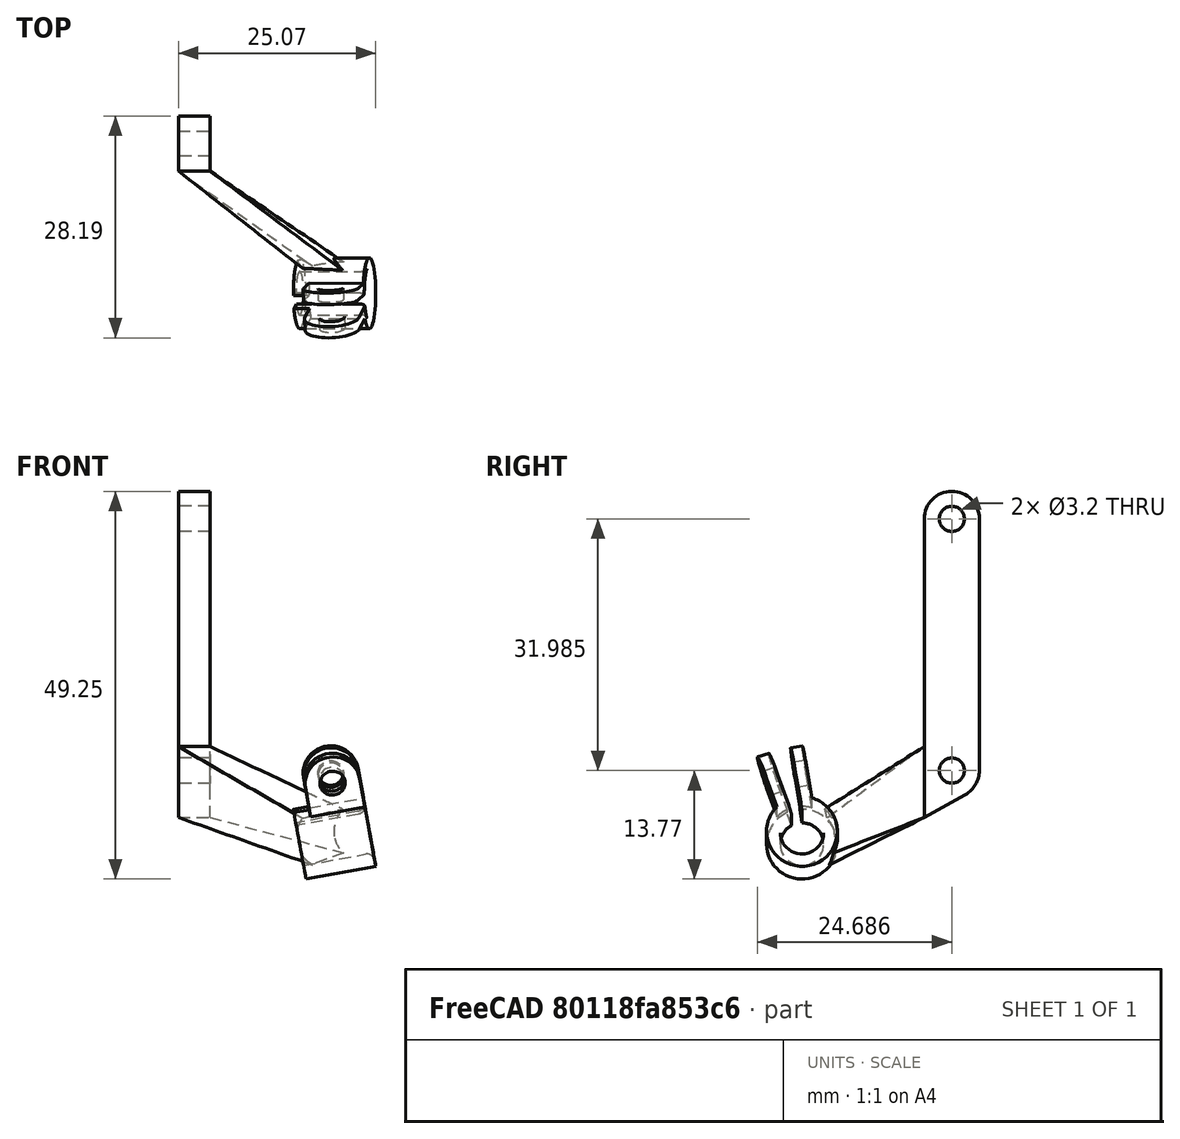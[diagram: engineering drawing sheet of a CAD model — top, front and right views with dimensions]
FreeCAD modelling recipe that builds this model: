
FCSTD DOCUMENT  (FreeCAD 0.19R21097 (Git))
Label: mount
License: All rights reserved
LicenseURL: http://en.wikipedia.org/wiki/All_rights_reserved
objects: Sketcher::SketchObject×8, PartDesign::Plane×6, Part::Extrusion×4, Part::MultiFuse×2, Mesh::Feature×1, Part::Feature×1, PartDesign::Pad×1, PartDesign::Body×1, Part::Sweep×1, Part::Cut×1, Part::Fillet×1
note: 27 computed .brp shape members not serialized (recipe doc carries the construction recipe); baked Part::Feature solids carry a one-line shape summary decoded from their .brp

FEATURE [Mesh::Feature] MK3S_nozzle_camera_mount_screw_tight
  Placement = pos=(-2,363,-102) rot=(0,0,1;3.14159rad)
FEATURE [Sketcher::SketchObject] Sketch  label="base arm top"
  MapMode = 5
  Placement = pos=(0,0,0) rot=(0.57735,0.57735,0.57735;2.0944rad)
  Support = -> [YZ_Plane]
  sketch-geometry (7):
    g0: Circle CenterX=3.46624 CenterY=28.9348 CenterZ=0 NormalX=0 NormalY=0 NormalZ=1 AngleXU=0 Radius=1.6
    g1: Circle CenterX=3.46624 CenterY=-3.05053 CenterZ=0 NormalX=0 NormalY=0 NormalZ=1 AngleXU=0 Radius=1.6
    g2: LineSegment StartX=-0.03376 StartY=28.9348 StartZ=0 EndX=-0.03376 EndY=-9.00443 EndZ=0
    g3: LineSegment StartX=6.96624 StartY=28.9348 StartZ=0 EndX=6.96624 EndY=-3.05053 EndZ=0
    g4: ArcOfCircle CenterX=3.46624 CenterY=28.9348 CenterZ=0 NormalX=0 NormalY=0 NormalZ=1 AngleXU=0 Radius=3.5 StartAngle=0 EndAngle=3.14159
    g5: ArcOfCircle CenterX=3.46624 CenterY=-3.05053 CenterZ=0 NormalX=0 NormalY=0 NormalZ=1 AngleXU=0 Radius=3.5 StartAngle=5.22031 EndAngle=6.28319
    g6: LineSegment StartX=-0.03376 StartY=-9.00443 StartZ=0 EndX=5.16851 EndY=-6.10868 EndZ=0
  constraints (18):
    c: Equal(g0,g1) = 3.2
    c: Vertical(g2)
    c: Vertical(g3)
    c: Horizontal(g3,g0)
    c: Horizontal(g0,g2)
    c: Coincident(g5,g1)
    c: Coincident(g3,g4)
    c: Coincident(g2,g4)
    c: Coincident(g4,g0)
    c: DistanceX(g0,g3) = 3.5
    c: Vertical(g0,g1)
    c: Diameter(g1) = 3.2
    c: Tangent(g5,g3) = 1.5708
    c: Coincident(g6,g2)
    c: Tangent(g6,g5) = -1.5708
    c: DistanceX(g0) = 3.46624
    c: DistanceY(g0) = 28.9348
    c: DistanceY(g1) = -3.05053
FEATURE [Part::Feature] MK3S_nozzle_camera_mount_screw_tight001
  Placement = pos=(6.10201,-725.648,-5.94582) rot=(0,0,1;0rad)
  shape: bbox 25.16 x 32.85 x 50.81 mm, 5956 faces, 0 solids (baked)
FEATURE [PartDesign::Plane] DatumPlane  label="DatumPlane grab top"
  AttachmentOffset = pos=(-24,-30,-2) rot=(0.379352,0.080641,0.921732;0.453327rad)
  Length = 87.983
  MapMode = 45
  Placement = pos=(26.7496,-49.7619,-24.5712) rot=(0.538842,0.541154,0.645602;1.98935rad)
  ResizeMode = 0
  Support = -> [MK3S_nozzle_camera_mount_screw_tight001]
  Width = 71.6948
FEATURE [Sketcher::SketchObject] Sketch001  label="grab top"
  MapMode = 5
  Placement = pos=(26.7496,-49.7619,-24.5712) rot=(0.538842,0.541154,0.645602;1.98935rad)
  Support = -> [DatumPlane]
  sketch-geometry (6):
    g0: ArcOfCircle CenterX=34.1177 CenterY=14.2055 CenterZ=0 NormalX=0 NormalY=0 NormalZ=1 AngleXU=0 Radius=2.75 StartAngle=2.08555 EndAngle=7.85398
    g1: ArcOfCircle CenterX=34.1177 CenterY=14.2055 CenterZ=0 NormalX=0 NormalY=0 NormalZ=1 AngleXU=0 Radius=4.5 StartAngle=2.0182 EndAngle=7.92133
    g2: LineSegment StartX=34.1177 StartY=16.9555 StartZ=0 EndX=33.8148 EndY=18.6953 EndZ=0
    g3: LineSegment StartX=32.7638 StartY=16.5991 StartZ=0 EndX=32.1708 EndY=18.2626 EndZ=0
    g4: LineSegment [constr] StartX=32.1708 StartY=18.2626 StartZ=0 EndX=33.8148 EndY=18.6953 EndZ=0
    g5: LineSegment [constr] StartX=32.7638 StartY=16.5991 StartZ=0 EndX=34.1177 EndY=16.9555 EndZ=0
  constraints (17):
    c: Diameter(g0) = 5.5
    c: Coincident(g1,g0)
    c: Diameter(g1) = 9
    c: DistanceX(g0) = 34.1177
    c: Coincident(g3,g0)
    c: Coincident(g1,g3)
    c: Coincident(g1,g2)
    c: Coincident(g4,g1)
    c: Coincident(g4,g1)
    c: Coincident(g5,g0)
    c: Coincident(g5,g0)
    c: Distance(g5) = 1.4
    c: Coincident(g2,g0)
    c: DistanceX(g0,g0) = 0
    c: Distance(g4) = 1.7
    c: Parallel(g5,g4)
    c: DistanceY(g0) = 14.2055
FEATURE [PartDesign::Pad] Pad
  AllowMultiFace = false
  Length = 9
  Length2 = 100
  Placement = pos=(26.7496,-49.7619,-24.5712) rot=(0.538842,0.541154,0.645602;1.98935rad)
  Profile = -> Sketch001
  Refine = true
  Reversed = true
  Type = 0
FEATURE [PartDesign::Plane] DatumPlane001  label="DatumPlane ear 1"
  Length = 64.7827
  MapMode = 13
  Placement = pos=(20.6775,-17.2949,-7.85855) rot=(0.999276,0.030966,0.022092;1.90294rad)
  ResizeMode = 0
  Support = -> [Pad,Sketch001]
  Width = 76.232
FEATURE [Sketcher::SketchObject] Sketch002  label="ear 1"
  ExternalGeometry = -> [Sketch001,Pad]
  MapMode = 5
  Placement = pos=(20.6775,-17.2949,-7.85855) rot=(0.999276,0.030966,0.022092;1.90294rad)
  Support = -> [DatumPlane001]
  sketch-geometry (8):
    g0: LineSegment StartX=2.83337 StartY=1.14826 StartZ=0 EndX=2.16798 EndY=4.58443 EndZ=0
    g1: ArcOfCircle CenterX=-1.26819 CenterY=3.91903 CenterZ=0 NormalX=0 NormalY=0 NormalZ=1 AngleXU=0 Radius=3.5 StartAngle=0.191278 EndAngle=3.33287
    g2: LineSegment StartX=-4.70436 StartY=3.25363 StartZ=0 EndX=-4.03896 EndY=-0.18254 EndZ=0
    g3: LineSegment [constr] StartX=-1.26819 StartY=3.91903 StartZ=0 EndX=-0.602792 EndY=0.48286 EndZ=0
    g4: Circle CenterX=-1.26819 CenterY=3.91903 CenterZ=0 NormalX=0 NormalY=0 NormalZ=1 AngleXU=0 Radius=1.6
    g5: LineSegment StartX=-4.03896 StartY=-0.18254 StartZ=0 EndX=-3.84885 EndY=-1.1643 EndZ=0
    g6: LineSegment StartX=-3.84885 StartY=-1.1643 StartZ=0 EndX=3.02349 EndY=0.166497 EndZ=0
    g7: LineSegment StartX=3.02349 StartY=0.166497 StartZ=0 EndX=2.83337 EndY=1.14826 EndZ=0
  constraints (21):
    c: Coincident(g0,g-4)
    c: Perpendicular(g0,g-4)
    c: Coincident(g0,g1)
    c: Tangent(g2,g1) = -1.5708
    c: Equal(g2,g0)
    c: Perpendicular(g-4,g2)
    c: Coincident(g3,g1)
    c: Perpendicular(g-4,g3)
    c: Equal(g0,g3)
    c: Coincident(g4,g1)
    c: Diameter(g4) = 3.2
    c: Distance(g1,g0) = 3.5
    c: Distance(g3) = 3.5
    c: PointOnObject(g2,g-4)
    c: Coincident(g6,g5)
    c: Coincident(g7,g6)
    c: Coincident(g7,g0)
    c: Tangent(g5,g2) = -1.5708
    c: Perpendicular(g5,g6)
    c: Perpendicular(g7,g6)
    c: Distance(g5) = 1
FEATURE [PartDesign::Plane] DatumPlane002  label="DatumPlane ear 2"
  Length = 62.432
  MapMode = 13
  Placement = pos=(17.6561,-15.7425,-8.00522) rot=(-0.009485,0.646658,0.762722;3.16397rad)
  ResizeMode = 0
  Support = -> [Pad]
  Width = 68.6517
FEATURE [Sketcher::SketchObject] Sketch003  label="ear 2"
  ExternalGeometry = -> [Pad]
  MapMode = 5
  Placement = pos=(17.6561,-15.7425,-8.00522) rot=(-0.009485,0.646658,0.762722;3.16397rad)
  Support = -> [DatumPlane002]
  sketch-geometry (10):
    g0: LineSegment StartX=-5.79228 StartY=1.67212 StartZ=0 EndX=-5.15451 EndY=5.11352 EndZ=0
    g1: LineSegment StartX=1.09052 StartY=0.396576 StartZ=0 EndX=1.7283 EndY=3.83798 EndZ=0
    g2: ArcOfCircle CenterX=-1.71311 CenterY=4.47575 CenterZ=0 NormalX=0 NormalY=0 NormalZ=1 AngleXU=0 Radius=3.5 StartAngle=6.09994 EndAngle=9.24153
    g3: LineSegment [constr] StartX=-1.71311 StartY=4.47575 StartZ=0 EndX=-2.35088 EndY=1.03435 EndZ=0
    g4: Circle CenterX=-1.71311 CenterY=4.47575 CenterZ=0 NormalX=0 NormalY=0 NormalZ=1 AngleXU=0 Radius=1.6
    g5: LineSegment StartX=-5.79228 StartY=1.67212 StartZ=0 EndX=-6.06561 EndY=0.197236 EndZ=0
    g6: LineSegment StartX=-6.06561 StartY=0.197236 StartZ=0 EndX=0.817191 EndY=-1.07831 EndZ=0
    g7: LineSegment StartX=0.817191 StartY=-1.07831 StartZ=0 EndX=1.09052 EndY=0.396576 EndZ=0
    g8: LineSegment [constr] StartX=-1.71311 StartY=4.47575 StartZ=0 EndX=1.7283 EndY=3.83798 EndZ=0
    g9: LineSegment [constr] StartX=-5.15451 StartY=5.11352 StartZ=0 EndX=-1.71311 EndY=4.47575 EndZ=0
  constraints (25):
    c: Coincident(g0,g-3)
    c: PointOnObject(g1,g-3)
    c: Equal(g0,g1)
    c: Coincident(g2,g0)
    c: Coincident(g2,g1)
    c: Coincident(g3,g2)
    c: Distance(g3) = 3.5
    c: Equal(g1,g3)
    c: Distance(g2,g1) = 3.5
    c: Coincident(g4,g2)
    c: Diameter(g4) = 3.2
    c: Coincident(g6,g5)
    c: Coincident(g7,g6)
    c: Tangent(g5,g0) = 1.5708
    c: Perpendicular(g6,g5)
    c: Perpendicular(g7,g6)
    c: Tangent(g7,g1) = -1.5708
    c: Distance(g5) = 1.5
    c: Distance(g7) = 1.5
    c: Coincident(g8,g2)
    c: Coincident(g8,g1)
    c: Perpendicular(g3,g8)
    c: Coincident(g9,g2)
    c: Perpendicular(g3,g9)
    c: Coincident(g9,g0)
FEATURE [Part::Extrusion] Extrude  label="solid ear 1"
  Base = -> Sketch002
  Dir = (0.0585479,-0.943755,-0.325422)
  DirMode = 2
  FaceMakerClass = Part::FaceMakerBullseye
  LengthFwd = 1.5
  LengthRev = 0
  Solid = true
  Symmetric = false
FEATURE [Part::Extrusion] Extrude001  label="solid ear 2"
  Base = -> Sketch003
  Dir = (-0.0289335,0.986104,0.163593)
  DirMode = 2
  FaceMakerClass = Part::FaceMakerBullseye
  LengthFwd = 1.5
  LengthRev = 0
  Solid = true
  Symmetric = false
FEATURE [Part::Extrusion] Extrude002  label="solid base arm"
  Base = -> Sketch
  Dir = (1,-1e-16,1e-16)
  DirMode = 2
  FaceMakerClass = Part::FaceMakerBullseye
  LengthFwd = 4
  LengthRev = 0
  Solid = true
  Symmetric = false
FEATURE [Sketcher::SketchObject] Sketch004  label="diagonal arm cross 1"
  ExternalGeometry = -> [Sketch]
  MapMode = 5
  Placement = pos=(0,-0.03376,0) rot=(1,0,0;1.5708rad)
  Support = -> [Extrude002]
  sketch-geometry (4):
    g0: LineSegment StartX=2e-15 StartY=-9.00443 StartZ=0 EndX=4 EndY=-9.00443 EndZ=0
    g1: LineSegment StartX=4 StartY=-9.00443 StartZ=0 EndX=4 EndY=0 EndZ=0
    g2: LineSegment StartX=4 StartY=0 StartZ=0 EndX=0 EndY=0 EndZ=0
    g3: LineSegment StartX=0 StartY=0 StartZ=0 EndX=2e-15 EndY=-9.00443 EndZ=0
  constraints (10):
    c: Coincident(g0,g1)
    c: Coincident(g1,g2)
    c: Coincident(g2,g3)
    c: Coincident(g3,g0)
    c: Horizontal(g0)
    c: Horizontal(g2)
    c: Vertical(g1)
    c: Coincident(g2,g-1)
    c: Coincident(g0,g-3)
    c: DistanceX(g0,g0) = 4
FEATURE [PartDesign::Plane] DatumPlane003
  AttachmentOffset = pos=(0,0,13) rot=(0,0,1;0rad)
  Length = 60.086
  MapMode = 5
  Placement = pos=(0,-13,-2.9e-15) rot=(1,0,0;1.5708rad)
  ResizeMode = 0
  Support = -> [XZ_Plane]
  Width = 60.0078
FEATURE [Sketcher::SketchObject] Sketch005  label="diagonal arm cross 2"
  MapMode = 5
  Placement = pos=(0,-13,-2.9e-15) rot=(1,0,0;1.5708rad)
  Support = -> [DatumPlane003]
  sketch-geometry (4):
    g0: LineSegment StartX=16.5372 StartY=-9.54211 StartZ=0 EndX=21.3331 EndY=-8.12806 EndZ=0
    g1: LineSegment StartX=23.0811 StartY=-14.0567 StartZ=0 EndX=18.2852 EndY=-15.4707 EndZ=0
    g2: LineSegment StartX=18.2852 StartY=-15.4707 StartZ=0 EndX=16.5372 EndY=-9.54211 EndZ=0
    g3: LineSegment StartX=21.3331 StartY=-8.12806 StartZ=0 EndX=23.0811 EndY=-14.0567 EndZ=0
  constraints (8):
    c: Coincident(g2,g1)
    c: Coincident(g2,g0)
    c: Coincident(g3,g0)
    c: Coincident(g3,g1)
    c: Perpendicular(g3,g0)
    c: Equal(g1,g0)
    c: Perpendicular(g3,g1)
    c: Distance(g0) = 5
FEATURE [PartDesign::Plane] DatumPlane004
  Length = 81.5849
  MapMode = 13
  Placement = pos=(6.09508,-4.35584,1.48653) rot=(0.911741,-0.290455,-0.290455;1.66306rad)
  ResizeMode = 0
  Support = -> [Sketch,Sketch005]
  Width = 61.8129
FEATURE [Sketcher::SketchObject] Sketch006  label="diagonal arm path"
  ExternalGeometry = -> [Sketch005,Sketch004,Sketch]
  MapMode = 5
  Placement = pos=(6.09508,-4.35584,1.48653) rot=(0.911741,-0.290455,-0.290455;1.66306rad)
  Support = -> [DatumPlane004]
  sketch-geometry (1):
    g0: LineSegment StartX=-7.47197 StartY=-10.491 StartZ=0 EndX=14.9439 EndY=-16.9573 EndZ=0
  constraints (2):
    c: Coincident(g0,g-5)
    c: Coincident(g0,g-8)
FEATURE [PartDesign::Plane] DatumPlane005
  Length = 87.983
  MapMode = 2
  Placement = pos=(26.7496,-49.7619,-24.5712) rot=(0.538842,0.541154,0.645602;1.98935rad)
  ResizeMode = 0
  Support = -> [Sketch001]
  Width = 71.6948
FEATURE [Sketcher::SketchObject] Sketch007  label="grab top hole"
  ExternalGeometry = -> [Pad]
  MapMode = 5
  Placement = pos=(26.7496,-49.7619,-24.5712) rot=(0.538842,0.541154,0.645602;1.98935rad)
  Support = -> [DatumPlane005]
  sketch-geometry (1):
    g0: Circle CenterX=34.1177 CenterY=14.2055 CenterZ=0 NormalX=0 NormalY=0 NormalZ=1 AngleXU=0 Radius=2.75
  constraints (2):
    c: Coincident(g0,g-3)
    c: PointOnObject(g-3,g0)
FEATURE [PartDesign::Body] Body
  Group = -> [Sketch,DatumPlane,Sketch001,Pad,DatumPlane001,Sketch002,DatumPlane002,Sketch003,Sketch004,DatumPlane003,Sketch005,DatumPlane004,Sketch006,DatumPlane005,Sketch007]
  Origin = -> Origin
  Tip = -> Pad
FEATURE [Part::Extrusion] Extrude003  label="solid grab hole"
  Base = -> Sketch007
  Dir = (0.983709,-0.000959639,0.179766)
  DirMode = 2
  FaceMakerClass = Part::FaceMakerBullseye
  LengthFwd = 23
  LengthRev = 0
  Solid = true
  Symmetric = true
FEATURE [Part::Sweep] Sweep  label="solid diagonal arm"
  Frenet = true
  Sections = -> [Sketch004,Sketch005]
  Solid = true
  Spine = -> Sketch006 [Edge1]
  Transition = 1
FEATURE [Part::Cut] Cut  label="solid diagonal arm without hole"
  Base = -> Sweep
  Refine = true
  Tool = -> Extrude003
FEATURE [Part::MultiFuse] Fusion  label="body plus ears"
  Refine = true
  Shapes = -> [Extrude,Body,Extrude001]
FEATURE [Part::MultiFuse] Fusion001  label="full mount"
  Refine = true
  Shapes = -> [Fusion,Cut,Extrude002]
FEATURE [Part::Fillet] Fillet
  Base = -> Fusion001
  Edges = 1 edges r=1: [Edge58]
